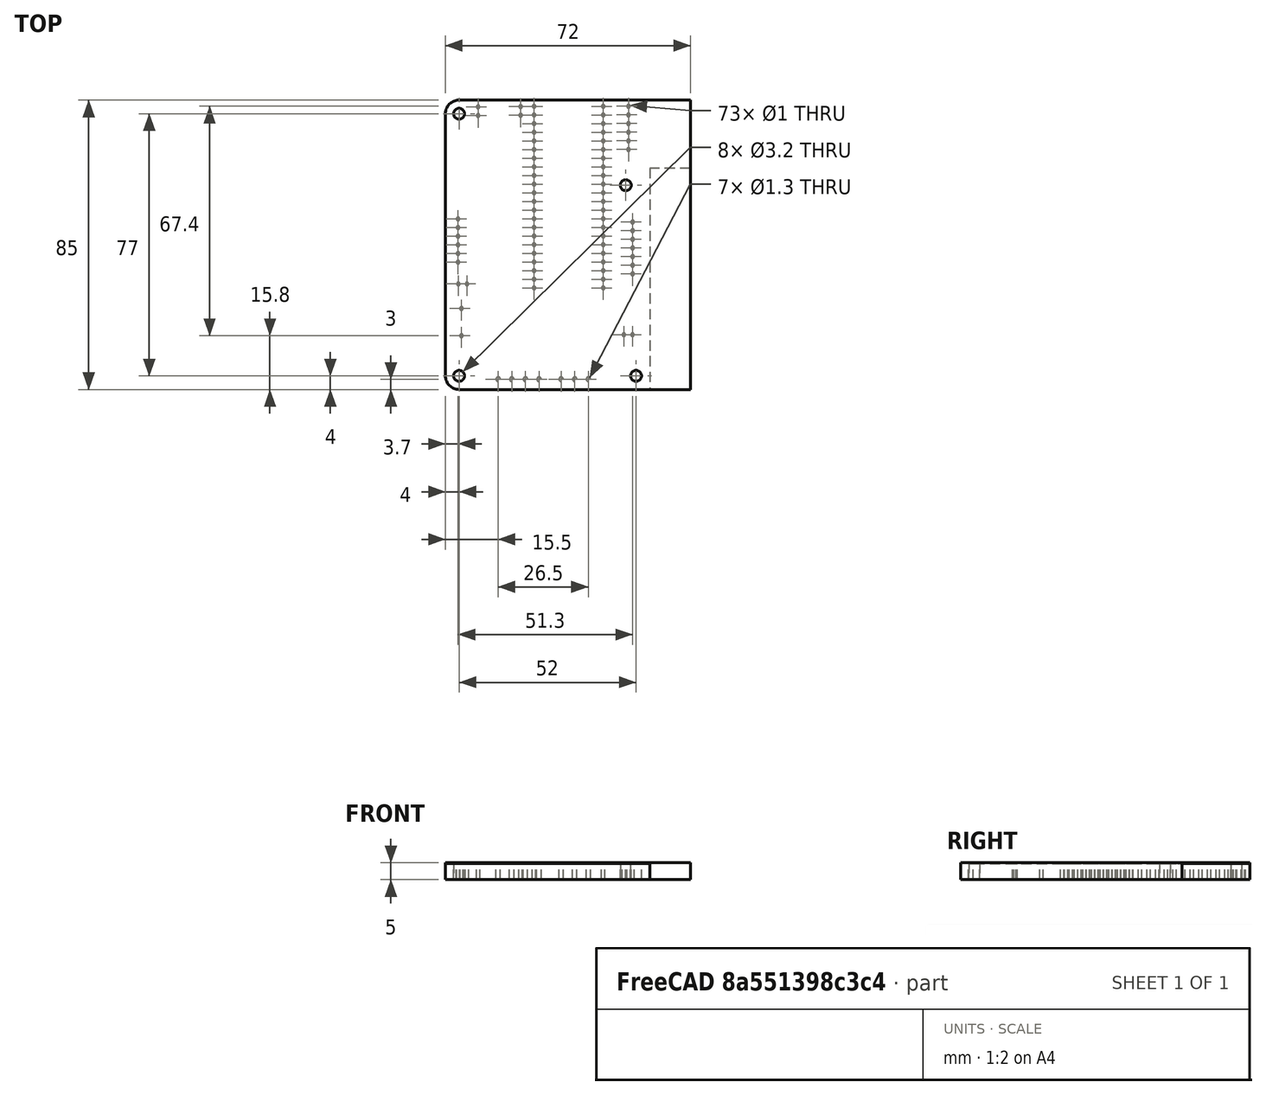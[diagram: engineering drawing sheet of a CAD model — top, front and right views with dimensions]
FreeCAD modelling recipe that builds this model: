
FCSTD DOCUMENT  (FreeCAD 0.18.4R)
Label: GbSwitchFp_haut
License: All rights reserved
LicenseURL: http://en.wikipedia.org/wiki/All_rights_reserved
objects: Part::Feature×1, Sketcher::SketchObject×1, Part::Extrusion×1
note: 3 computed .brp shape members not serialized (recipe doc carries the construction recipe); baked Part::Feature solids carry a one-line shape summary decoded from their .brp

FEATURE [Part::Feature] Solid  label="GbSwitchFp 1"
  shape: bbox 72 x 85 x 4.69 mm, 94 faces (baked)
FEATURE [Sketcher::SketchObject] Sketch
  ExternalGeometry = -> [Solid]
  MapMode = 2
  Support = -> [Solid]
  sketch-geometry (10):
    g0: Circle CenterX=4 CenterY=-4 CenterZ=0 NormalX=0 NormalY=0 NormalZ=1 AngleXU=0 Radius=1.6
    g1: Circle CenterX=53 CenterY=-25 CenterZ=0 NormalX=0 NormalY=0 NormalZ=1 AngleXU=0 Radius=1.6
    g2: Circle CenterX=4 CenterY=-81 CenterZ=0 NormalX=0 NormalY=0 NormalZ=1 AngleXU=0 Radius=1.6
    g3: Circle CenterX=56 CenterY=-81 CenterZ=0 NormalX=0 NormalY=0 NormalZ=1 AngleXU=0 Radius=1.6
    g4: LineSegment StartX=0 StartY=-4 StartZ=0 EndX=0 EndY=-81 EndZ=0
    g5: LineSegment StartX=4 StartY=-85 StartZ=0 EndX=72 EndY=-85 EndZ=0
    g6: LineSegment StartX=4 StartY=0 StartZ=0 EndX=72 EndY=0 EndZ=0
    g7: LineSegment StartX=72 StartY=0 StartZ=0 EndX=72 EndY=-85 EndZ=0
    g8: ArcOfCircle CenterX=4 CenterY=-4 CenterZ=0 NormalX=0 NormalY=0 NormalZ=1 AngleXU=0 Radius=4 StartAngle=1.5708 EndAngle=3.14159
    g9: ArcOfCircle CenterX=4 CenterY=-81 CenterZ=0 NormalX=0 NormalY=0 NormalZ=1 AngleXU=0 Radius=4 StartAngle=3.14159 EndAngle=4.71239
  constraints (15):
    c: Coincident(g0,g-9)
    c: Coincident(g1,g-10)
    c: Coincident(g2,g-11)
    c: Coincident(g3,g-12)
    c: Coincident(g4,g-7)
    c: Coincident(g4,g-6)
    c: Coincident(g5,g-5)
    c: Coincident(g6,g-8)
    c: Coincident(g6,g-8)
    c: Coincident(g7,g6)
    c: Coincident(g7,g5)
    c: Coincident(g8,g6)
    c: Coincident(g8,g4)
    c: Coincident(g5,g9)
    c: Coincident(g9,g4)
FEATURE [Part::Extrusion] Extrude
  Base = -> Sketch
  Dir = (0,0,1)
  DirMode = 2
  FaceMakerClass = Part::FaceMakerBullseye
  LengthFwd = 5
  LengthRev = 0
  Solid = true
  Symmetric = false
